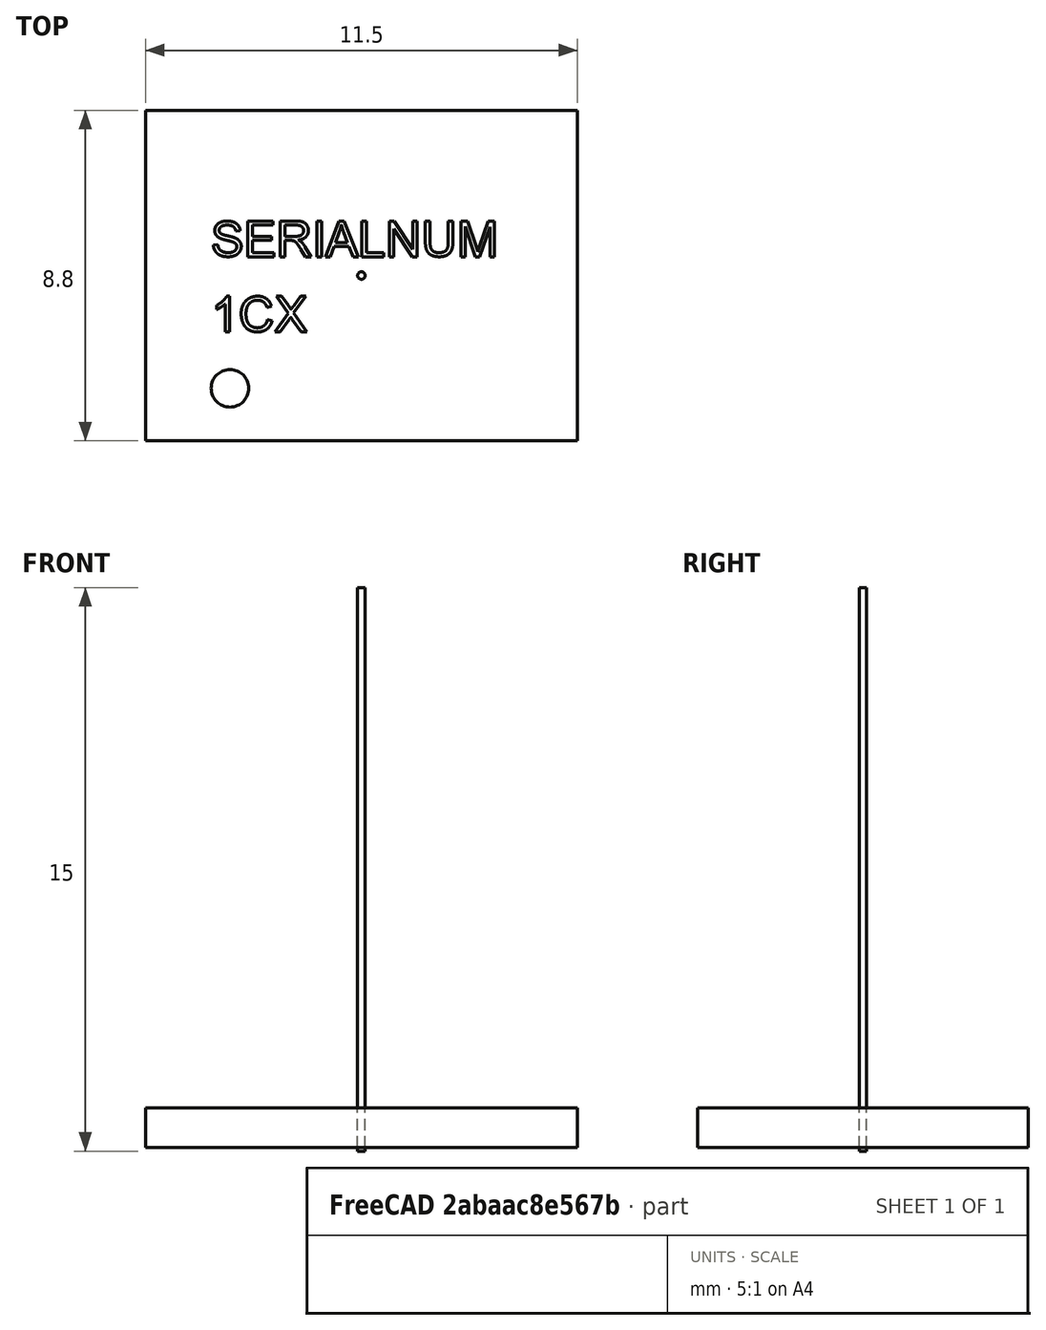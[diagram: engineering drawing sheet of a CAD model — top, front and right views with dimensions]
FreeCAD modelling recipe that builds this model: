
FCSTD DOCUMENT  (FreeCAD 0.18R4 (GitTag))
Label: 1CX
License: All rights reserved
LicenseURL: http://en.wikipedia.org/wiki/All_rights_reserved
objects: Part::Cut×13, Part::Feature×12, Part::Extrusion×12, Part::Cylinder×2, Part::Part2DObjectPython×2, Part::Box×1
note: 42 computed .brp shape members not serialized (recipe doc carries the construction recipe); baked Part::Feature solids carry a one-line shape summary decoded from their .brp

FEATURE [Part::Box] Box  label="Cube"
  AttacherType = Attacher::AttachEngine3D
  Height = 1.05
  Length = 11.5
  Placement = pos=(-5.75,-4.4,0.1) rot=(0,0,1;0rad)
  Width = 8.8
  expr: Placement.Base.y = -(Width / 2)
  expr: Placement.Base.x = -(Length / 2)
FEATURE [Part::Cylinder] Cylinder
  Angle = 360
  AttacherType = Attacher::AttachEngine3D
  Height = 15
  Radius = 0.1
FEATURE [Part::Part2DObjectPython] ShapeString  # Draft 2D object (typed FeaturePython)
  FontFile = C:/Program Files/FreeCAD 0.18/fonts/arial.ttf
  Placement = pos=(-4,0.5,1.15) rot=(0,0,1;0rad)
  Size = 1
  String = SERIALNUM
  Tracking = 0
FEATURE [Part::Part2DObjectPython] ShapeString001  # Draft 2D object (typed FeaturePython)
  FontFile = C:/Program Files/FreeCAD 0.18/fonts/arial.ttf
  Placement = pos=(-4,-1.5,1.15) rot=(0,0,1;0rad)
  Size = 1
  String = 1CX
  Tracking = 0
FEATURE [Part::Cylinder] Cylinder001
  Angle = 360
  AttacherType = Attacher::AttachEngine3D
  Height = 0.01
  Placement = pos=(-3.5,-3,1.14) rot=(0,0,1;0rad)
  Radius = 0.5
FEATURE [Part::Feature] Face
  Placement = pos=(-4,-1.5,1.15) rot=(0,0,1;0rad)
  shape: bbox 0.3439 x 0.9512 x 2e-07 mm, 1 faces, 0 solids (baked)
FEATURE [Part::Extrusion] Extrusion
  Base = -> Face
  Dir = (0,0,-0.01)
  DirMode = 0
  FaceMakerClass = Part::FaceMakerBullseye
  LengthFwd = 0
  LengthRev = 0
  Solid = true
  Symmetric = false
FEATURE [Part::Feature] Face001
  Placement = pos=(-4,-1.5,1.15) rot=(0,0,1;0rad)
  shape: bbox 0.8255 x 0.9512 x 2e-07 mm, 1 faces, 0 solids (baked)
FEATURE [Part::Extrusion] Extrusion001
  Base = -> Face001
  Dir = (0,0,-0.01)
  DirMode = 0
  FaceMakerClass = Part::FaceMakerBullseye
  LengthFwd = 0
  LengthRev = 0
  Solid = true
  Symmetric = false
FEATURE [Part::Feature] Face002
  Placement = pos=(-4,-1.5,1.15) rot=(0,0,1;0rad)
  shape: bbox 0.8561 x 0.9512 x 2e-07 mm, 1 faces, 0 solids (baked)
FEATURE [Part::Extrusion] Extrusion002
  Base = -> Face002
  Dir = (0,0,-0.01)
  DirMode = 0
  FaceMakerClass = Part::FaceMakerBullseye
  LengthFwd = 0
  LengthRev = 0
  Solid = true
  Symmetric = false
FEATURE [Part::Feature] Face003
  Placement = pos=(-4,0.5,1.15) rot=(0,0,1;0rad)
  shape: bbox 0.7435 x 0.9512 x 2e-07 mm, 1 faces, 0 solids (baked)
FEATURE [Part::Extrusion] Extrusion003
  Base = -> Face003
  Dir = (0,0,-0.01)
  DirMode = 0
  FaceMakerClass = Part::FaceMakerBullseye
  LengthFwd = 0
  LengthRev = 0
  Solid = true
  Symmetric = false
FEATURE [Part::Feature] Face004
  Placement = pos=(-4,0.5,1.15) rot=(0,0,1;0rad)
  shape: bbox 0.6968 x 0.9512 x 2e-07 mm, 1 faces, 0 solids (baked)
FEATURE [Part::Extrusion] Extrusion004
  Base = -> Face004
  Dir = (0,0,-0.01)
  DirMode = 0
  FaceMakerClass = Part::FaceMakerBullseye
  LengthFwd = 0
  LengthRev = 0
  Solid = true
  Symmetric = false
FEATURE [Part::Feature] Face005
  Placement = pos=(-4,0.5,1.15) rot=(0,0,1;0rad)
  shape: bbox 0.8229 x 0.9512 x 2e-07 mm, 1 faces, 0 solids (baked)
FEATURE [Part::Extrusion] Extrusion005
  Base = -> Face005
  Dir = (0,0,-0.01)
  DirMode = 0
  FaceMakerClass = Part::FaceMakerBullseye
  LengthFwd = 0
  LengthRev = 0
  Solid = true
  Symmetric = false
FEATURE [Part::Feature] Face006
  Placement = pos=(-4,0.5,1.15) rot=(0,0,1;0rad)
  shape: bbox 0.1236 x 0.9512 x 2e-07 mm, 1 faces, 0 solids (baked)
FEATURE [Part::Extrusion] Extrusion006
  Base = -> Face006
  Dir = (0,0,-0.01)
  DirMode = 0
  FaceMakerClass = Part::FaceMakerBullseye
  LengthFwd = 0
  LengthRev = 0
  Solid = true
  Symmetric = false
FEATURE [Part::Feature] Face007
  Placement = pos=(-4,0.5,1.15) rot=(0,0,1;0rad)
  shape: bbox 0.8743 x 0.9512 x 2e-07 mm, 1 faces, 0 solids (baked)
FEATURE [Part::Extrusion] Extrusion007
  Base = -> Face007
  Dir = (0,0,-0.01)
  DirMode = 0
  FaceMakerClass = Part::FaceMakerBullseye
  LengthFwd = 0
  LengthRev = 0
  Solid = true
  Symmetric = false
FEATURE [Part::Feature] Face008
  Placement = pos=(-4,0.5,1.15) rot=(0,0,1;0rad)
  shape: bbox 0.5834 x 0.9512 x 2e-07 mm, 1 faces, 0 solids (baked)
FEATURE [Part::Extrusion] Extrusion008
  Base = -> Face008
  Dir = (0,0,-0.01)
  DirMode = 0
  FaceMakerClass = Part::FaceMakerBullseye
  LengthFwd = 0
  LengthRev = 0
  Solid = true
  Symmetric = false
FEATURE [Part::Feature] Face009
  Placement = pos=(-4,0.5,1.15) rot=(0,0,1;0rad)
  shape: bbox 0.7359 x 0.9512 x 2e-07 mm, 1 faces, 0 solids (baked)
FEATURE [Part::Extrusion] Extrusion009
  Base = -> Face009
  Dir = (0,0,-0.01)
  DirMode = 0
  FaceMakerClass = Part::FaceMakerBullseye
  LengthFwd = 0
  LengthRev = 0
  Solid = true
  Symmetric = false
FEATURE [Part::Feature] Face010
  Placement = pos=(-4,0.5,1.15) rot=(0,0,1;0rad)
  shape: bbox 0.7342 x 0.9512 x 2e-07 mm, 1 faces, 0 solids (baked)
FEATURE [Part::Extrusion] Extrusion010
  Base = -> Face010
  Dir = (0,0,-0.01)
  DirMode = 0
  FaceMakerClass = Part::FaceMakerBullseye
  LengthFwd = 0
  LengthRev = 0
  Solid = true
  Symmetric = false
FEATURE [Part::Feature] Face011
  Placement = pos=(-4,0.5,1.15) rot=(0,0,1;0rad)
  shape: bbox 0.8913 x 0.9512 x 2e-07 mm, 1 faces, 0 solids (baked)
FEATURE [Part::Extrusion] Extrusion011
  Base = -> Face011
  Dir = (0,0,-0.01)
  DirMode = 0
  FaceMakerClass = Part::FaceMakerBullseye
  LengthFwd = 0
  LengthRev = 0
  Solid = true
  Symmetric = false
FEATURE [Part::Cut] Cut
  Base = -> Box
  Tool = -> Cylinder001
FEATURE [Part::Cut] Cut001
  Base = -> Cut
  Tool = -> Extrusion
FEATURE [Part::Cut] Cut002
  Base = -> Cut001
  Tool = -> Extrusion011
FEATURE [Part::Cut] Cut003
  Base = -> Cut002
  Tool = -> Extrusion010
FEATURE [Part::Cut] Cut004
  Base = -> Cut003
  Tool = -> Extrusion009
FEATURE [Part::Cut] Cut005
  Base = -> Cut004
  Tool = -> Extrusion008
FEATURE [Part::Cut] Cut006
  Base = -> Cut005
  Tool = -> Extrusion007
FEATURE [Part::Cut] Cut007
  Base = -> Cut006
  Tool = -> Extrusion006
FEATURE [Part::Cut] Cut008
  Base = -> Cut007
  Tool = -> Extrusion001
FEATURE [Part::Cut] Cut009
  Base = -> Cut008
  Tool = -> Extrusion002
FEATURE [Part::Cut] Cut010
  Base = -> Cut009
  Tool = -> Extrusion003
FEATURE [Part::Cut] Cut011
  Base = -> Cut010
  Tool = -> Extrusion004
FEATURE [Part::Cut] Cut012
  Base = -> Cut011
  Tool = -> Extrusion005
